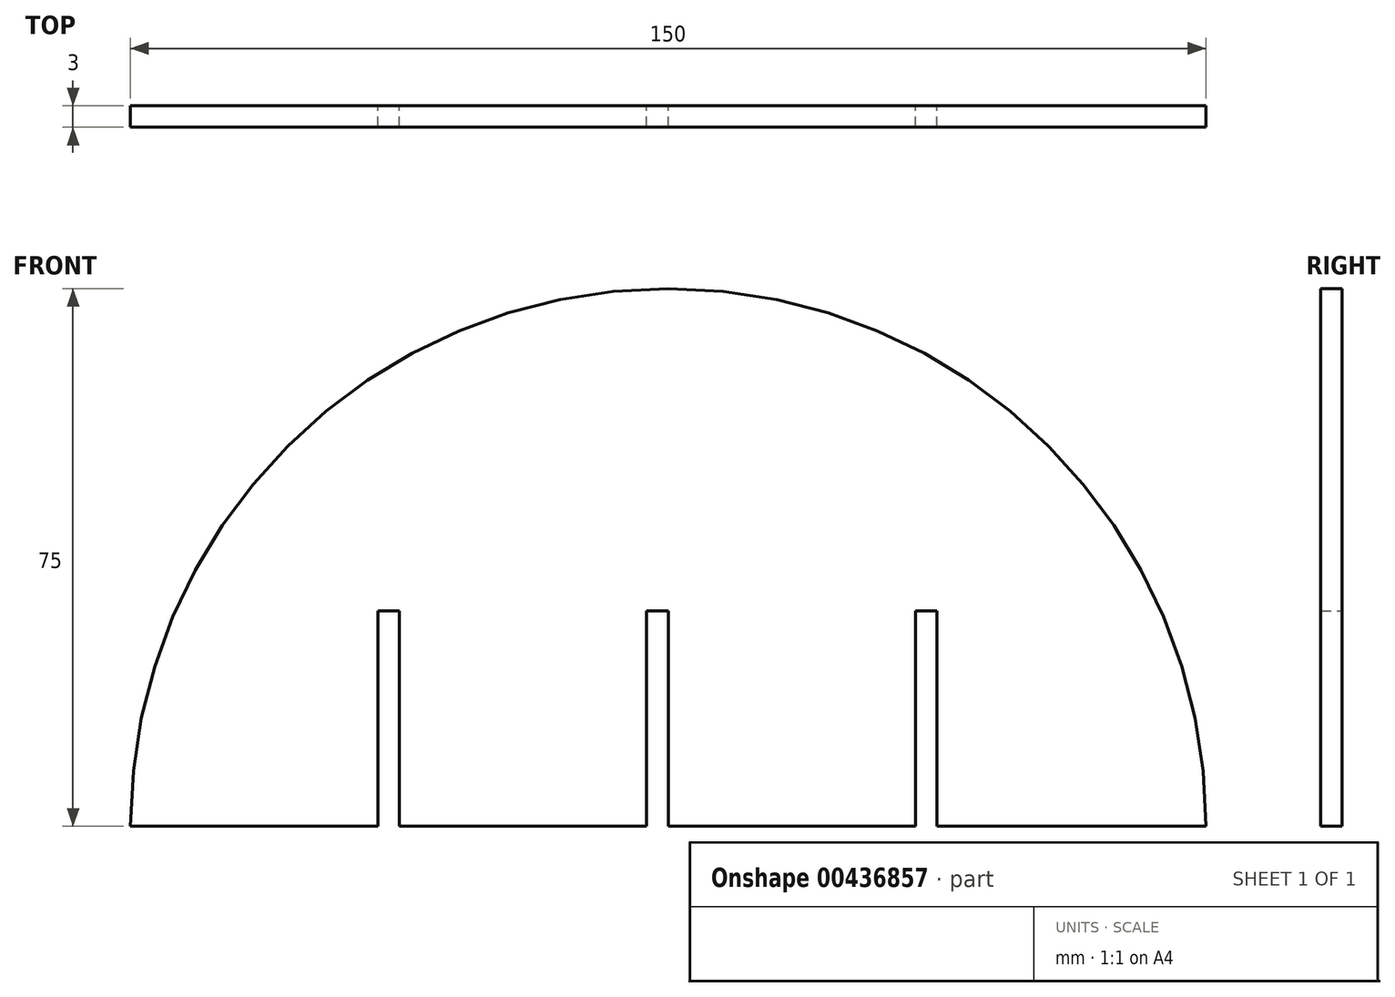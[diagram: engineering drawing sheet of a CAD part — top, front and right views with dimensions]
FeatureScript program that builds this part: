
annotation { "Feature Type Name" : "Feature", "Feature Type Description" : "" }
export const myFeature = defineFeature(function(context is Context, id is Id, definition is map)
    precondition{}
    {
        {
            var Q0;
            Q0=qCreatedBy(makeId("Front.planeOp"),FACE);
            var sketch = newSketch(context, id + "F0", { "sketchPlane" : qUnion([Q0])});
            skPoint(sketch, "E0.end.orphan", {"position": v(-75, 0) * mm});
            skPoint(sketch, "E1.start.orphan", {"position": v(75, 0) * mm});
            skLineSegment(sketch, "E2", {"start": v(75, 0) * mm, "end": v(37.5, 0) * mm});
            skArc(sketch, "E3", {"start": v(-75, 0) * mm, "mid": v(0, 75) * mm, "end": v(75, 0) * mm});
            skLineSegment(sketch, "E4", {"start": v(-75, 0) * mm, "end": v(-40.5, 0) * mm});
            skLineSegment(sketch, "E5", {"start": v(-37.5, 0) * mm, "end": v(-3, 0) * mm});
            skLineSegment(sketch, "E6", {"start": v(0, 0) * mm, "end": v(34.5, 0) * mm});
            skLineSegment(sketch, "E7", {"start": v(37.5, 0) * mm, "end": v(75, 0) * mm});
            skLineSegment(sketch, "E8", {"start": v(-37.5, 0) * mm, "end": v(-37.5, 30) * mm});
            skLineSegment(sketch, "E9", {"start": v(0, 0) * mm, "end": v(0, 30) * mm});
            skLineSegment(sketch, "E10", {"start": v(37.5, 0) * mm, "end": v(37.5, 30) * mm});
            skPoint(sketch, "E11", {"position": v(-40.5, 0) * mm});
            skPoint(sketch, "E12", {"position": v(-3, 0) * mm});
            skPoint(sketch, "E13", {"position": v(34.5, 0) * mm});
            skLineSegment(sketch, "E14", {"start": v(-40.5, 0) * mm, "end": v(-40.5, 30) * mm});
            skLineSegment(sketch, "E15", {"start": v(-40.5, 30) * mm, "end": v(-37.5, 30) * mm});
            skLineSegment(sketch, "E16", {"start": v(-3, 0) * mm, "end": v(-3, 30) * mm});
            skLineSegment(sketch, "E17", {"start": v(-3, 30) * mm, "end": v(0, 30) * mm});
            skLineSegment(sketch, "E18", {"start": v(34.5, 0) * mm, "end": v(34.5, 30) * mm});
            skLineSegment(sketch, "E19", {"start": v(34.5, 30) * mm, "end": v(37.5, 30) * mm});
            skLineSegment(sketch, "E20.trimOffspring", {"start": v(-40.5, 0) * mm, "end": v(-75, 0) * mm});
            skLineSegment(sketch, "E21.trimOffspring", {"start": v(-3, 0) * mm, "end": v(-37.5, 0) * mm});
            skLineSegment(sketch, "E22.trimOffspring", {"start": v(34.5, 0) * mm, "end": v(0, 0) * mm});
            skSolve(sketch);
        }
        {
            var Q0;
            Q0 = qSketchRegion(id + "F0", true);
            extrude(context, id + "F1", {"entities" : qUnion([Q0]), "depth" : 3 * mm, "offsetDistance" : 25 * mm});
        }
    });
